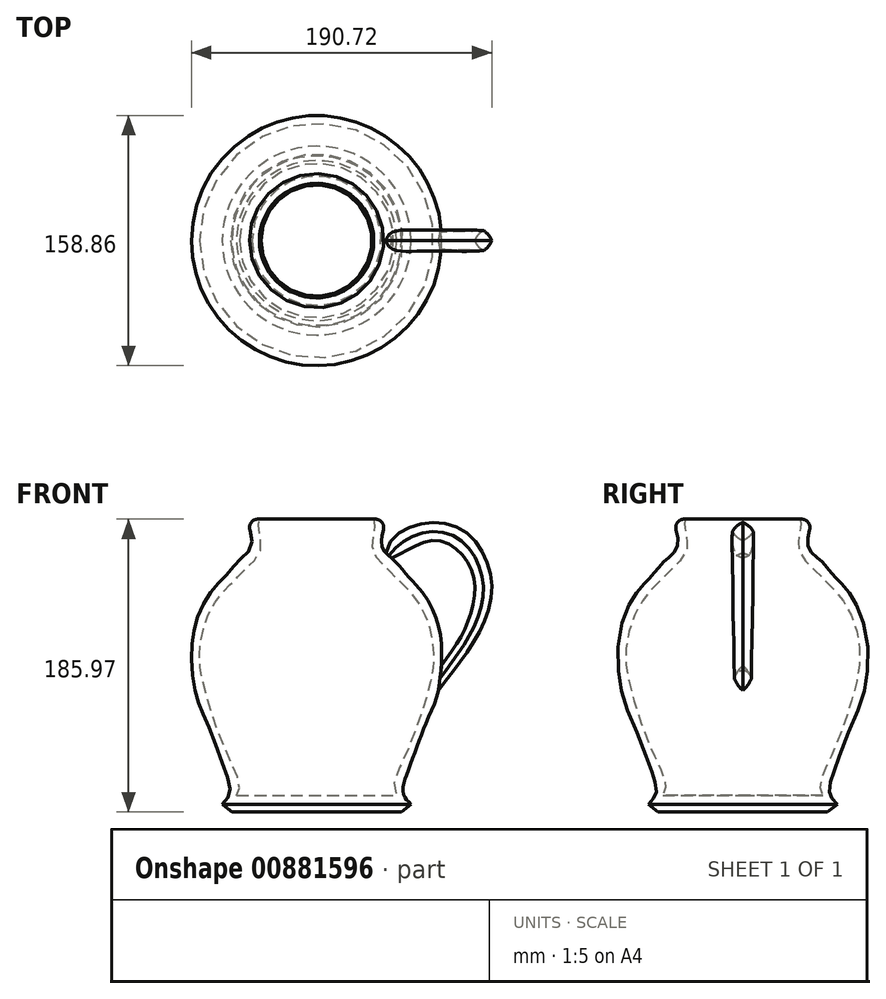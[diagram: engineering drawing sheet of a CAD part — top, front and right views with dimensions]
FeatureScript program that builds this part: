
annotation { "Feature Type Name" : "Feature", "Feature Type Description" : "" }
export const myFeature = defineFeature(function(context is Context, id is Id, definition is map)
    precondition{}
    {
        {
            var Q0;
            Q0=qCreatedBy(makeId("Front.planeOp"),FACE);
            var sketch = newSketch(context, id + "F0", { "sketchPlane" : qUnion([Q0])});
            skLineSegment(sketch, "E0", {"start": v(7.07, 103.51) * mm, "end": v(7.07, -101.49) * mm});
            skFitSpline(sketch, "E1", {"points": [v(152.31, 10.5) * mm, v(175.87, 42.7) * mm, v(187.4, 76.6) * mm, v(178.04, 105.94) * mm, v(165.53, 116.26) * mm, v(151.59, 119.63) * mm, v(136.93, 117.46) * mm, v(123.7, 110) * mm, v(118.66, 100.16) * mm], "startDerivative": vector(145.9, 183.09) * mm, "endDerivative": vector(-35.38, -119.28) * mm});
            skFitSpline(sketch, "E2", {"points": [v(154.96, 29.73) * mm, v(169.14, 52.56) * mm, v(174.9, 77.8) * mm, v(169.15, 95.12) * mm, v(155.48, 105.91) * mm, v(142.34, 105) * mm, v(132.6, 100.16) * mm, v(123.95, 95.59) * mm], "startDerivative": vector(86.52, 120.93) * mm, "endDerivative": vector(-79.67, -38.3) * mm});
            skLineSegment(sketch, "E3", {"start": v(118.66, 100.16) * mm, "end": v(123.95, 95.59) * mm});
            skLineSegment(sketch, "E4", {"start": v(154.96, 29.73) * mm, "end": v(152.31, 10.5) * mm});
            skSolve(sketch);
        }
        {
            var Q0;
            Q0=makeQuery(id+"F0.imprint","IMPRINT",FACE,{"disambiguationData":[TD([[makeQuery(id+"F0.imprint","IMPRINT",EDGE,{"derivedFrom":sQuery(id+"F0.wireOp",EDGE,"E1")}),1.0]])]});
            extrude(context, id + "F1", {"entities" : qUnion([Q0]), "endBound" : BoundingType.SYMMETRIC, "depth" : 16.5 * mm, "offsetDistance" : 25 * mm});
        }
        {
            var Q0;
            Q0=makeQuery(id+"F1.opExtrude","CAP_EDGE",EDGE,{"disambiguationData":[OSD([sQuery(id+"F0.wireOp",EDGE,"E1")])],"isStart":false});
            var Q1;
            Q1=makeQuery(id+"F1.opExtrude","CAP_EDGE",EDGE,{"disambiguationData":[OSD([sQuery(id+"F0.wireOp",EDGE,"E1")])],"isStart":true});
            var Q2;
            Q2=makeQuery(id+"F1.opExtrude","CAP_EDGE",EDGE,{"disambiguationData":[OSD([sQuery(id+"F0.wireOp",EDGE,"E2")])],"isStart":false});
            var Q3;
            Q3=makeQuery(id+"F1.opExtrude","CAP_EDGE",EDGE,{"disambiguationData":[OSD([sQuery(id+"F0.wireOp",EDGE,"E2")])],"isStart":true});
            fillet(context, id + "F2", {"entities" : qUnion([Q0, Q1, Q2, Q3]), "radius" : 12.8 * mm, "tangentPropagation" : true, "allowEdgeOverflow" : false});
        }
        {
            var Q0;
            Q0=qCreatedBy(makeId("Front.planeOp"),FACE);
            var sketch = newSketch(context, id + "F3", { "sketchPlane" : qUnion([Q0])});
            skFitSpline(sketch, "E5", {"points": [v(135.24, -60.12) * mm, v(130.35, -53.46) * mm, v(133.36, -38.92) * mm, v(145.61, -6.75) * mm, v(151.72, 8.5) * mm, v(154.71, 34.33) * mm, v(151.98, 55.22) * mm, v(142.7, 74.32) * mm, v(132.85, 85.25) * mm, v(124.12, 95.17) * mm, v(116.86, 103.23) * mm, v(118.66, 116.83) * mm, v(121.32, 120.93) * mm], "startDerivative": vector(-102.9, 100.17) * mm, "endDerivative": vector(45.41, 79.64) * mm});
            skFitSpline(sketch, "E6", {"points": [v(126.1, -54.6) * mm, v(124.3, -48.25) * mm, v(132.69, -26.7) * mm, v(142.67, 0) * mm, v(148.98, 24.82) * mm, v(149.24, 40.42) * mm, v(144.58, 58.9) * mm, v(135.04, 74.32) * mm, v(127.35, 82.07) * mm, v(117.81, 91.83) * mm, v(110.76, 102.1) * mm, v(112.27, 117.83) * mm, v(111.59, 120.93) * mm], "startDerivative": vector(-54.58, 99.39) * mm, "endDerivative": vector(-33.6, 67.99) * mm});
            skLineSegment(sketch, "E7", {"start": v(126.1, -54.6) * mm, "end": v(75.28, -54.6) * mm});
            skLineSegment(sketch, "E8", {"start": v(75.28, -54.6) * mm, "end": v(75.28, -65.04) * mm});
            skLineSegment(sketch, "E9", {"start": v(75.28, -65.04) * mm, "end": v(129.06, -65.04) * mm});
            skLineSegment(sketch, "E10", {"start": v(129.06, -65.04) * mm, "end": v(135.24, -60.12) * mm});
            skLineSegment(sketch, "E11", {"start": v(111.59, 120.93) * mm, "end": v(121.32, 120.93) * mm});
            skLineSegment(sketch, "E12", {"start": v(118.88, 99.8) * mm, "end": v(118.88, 99.8) * mm});
            skLineSegment(sketch, "E13", {"start": v(20.83, -64.54) * mm, "end": v(129.06, -65.04) * mm});
            skLineSegment(sketch, "E14", {"start": v(75.28, -65.04) * mm, "end": v(75.28, 121.11) * mm});
            skSolve(sketch);
        }
        {
            var Q0;
            Q0=makeQuery(id+"F3.imprint","IMPRINT",FACE,{"disambiguationData":[TD([[makeQuery(id+"F3.imprint","IMPRINT",EDGE,{"derivedFrom":sQuery(id+"F3.wireOp",EDGE,"E5")}),1.0]])]});
            var Q1;
            Q1=sQuery(id+"F3.wireOp",EDGE,"E14");
            revolve(context, id + "F4", {"operationType" : NewBodyOperationType.ADD, "surfaceOperationType" : NewSurfaceOperationType.NEW, "entities" : qUnion([Q0]), "axis" : qUnion([Q1]), "revolveType" : RevolveType.FULL});
        }
        {
            var Q0;
            Q0=makeQuery(id+"F4.opRevolve","SWEPT_EDGE",EDGE,{"disambiguationData":[OSD([sQuery(id+"F3.wireOp",EDGE,"E5"),sQuery(id+"F3.wireOp",EDGE,"E11")])]});
            fillet(context, id + "F5", {"entities" : qUnion([Q0]), "radius" : 5.15 * mm, "tangentPropagation" : true, "allowEdgeOverflow" : false});
        }
    });
